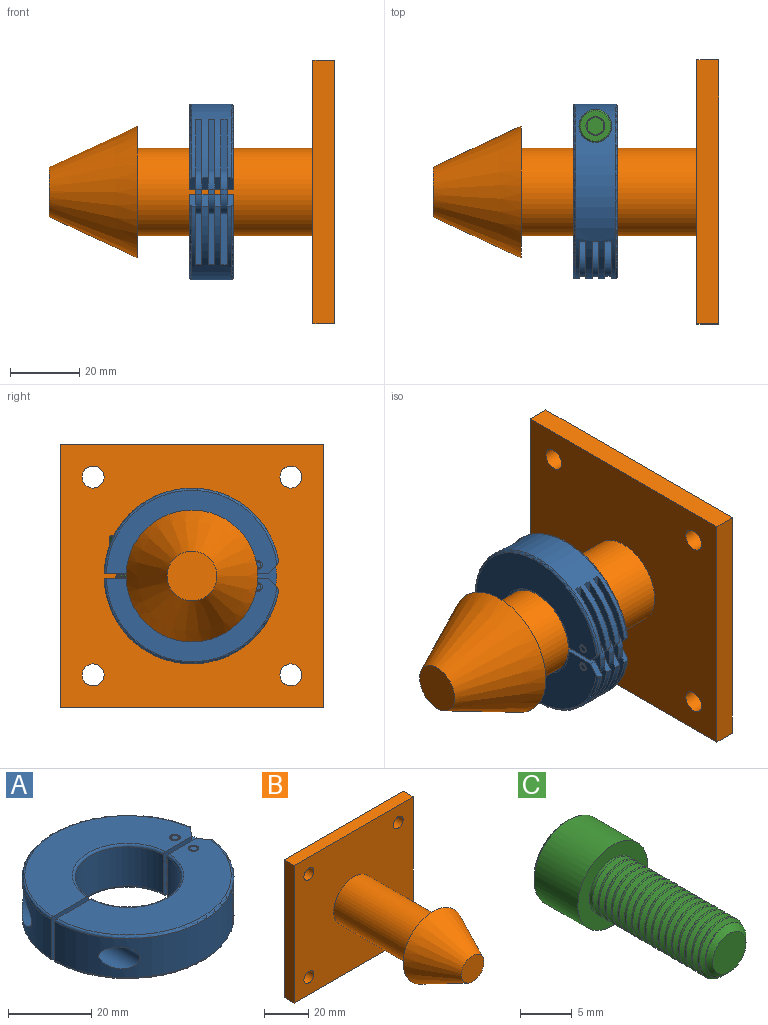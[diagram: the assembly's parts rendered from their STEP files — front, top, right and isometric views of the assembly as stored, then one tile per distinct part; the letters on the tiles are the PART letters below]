
ASSEMBLY  parts=3 mates=2
PART A: 80 faces, bbox 54.9x55.2x12.9 mm
  f0: cone r=0.89mm half-angle=45deg, axis (0,0,-1), area 3.7mm2, adj f10,f79
  f1: cone r=0.89mm half-angle=45deg, axis (0,0,1), area 3.7mm2, adj f9,f78
  f2: cone r=0.89mm half-angle=45deg, axis (0,0,-1), area 3.7mm2, adj f7,f77
  f3: cone r=0.89mm half-angle=45deg, axis (0,0,1), area 3.7mm2, adj f6,f76
  f4: cylinder r=3.17mm len=6.35mm, axis (0,-1,0), area 95mm2, adj f53,f55
  f5: cylinder r=4.76mm len=15.6mm, axis (0,-1,0), area 314.5mm2, adj f52,f55
  f6: cylinder r=1.27mm len=2.54mm, axis (0,0,-1), area 3mm2, adj f3,f51
  f7: cylinder r=1.27mm len=2.54mm, axis (0,0,-1), area 3mm2, adj f2,f50
  f8: cylinder r=3.17mm len=19.19mm, axis (0,-1,0), area 307.8mm2, adj f32,f35
  f9: cylinder r=1.27mm len=2.54mm, axis (0,0,-1), area 3mm2, adj f1,f31
  f10: cylinder r=1.27mm len=2.54mm, axis (0,0,-1), area 3mm2, adj f0,f30
  f11: plane 17.57x1.81mm, normal (1,0,0), area 31.9mm2, adj f12,f13,f32,f75
  f12: plane 18.16x10.8mm, normal (0,0,-1), area 106.4mm2, adj f11,f32,f42,f75
  f13: plane 18.16x10.8mm, normal (0,0,1), area 106.4mm2, adj f11,f32,f41,f75
  f14: plane 17.57x1.81mm, normal (1,0,0), area 31.9mm2, adj f15,f16,f52,f73
  f15: plane 18.16x10.8mm, normal (0,0,-1), area 106.4mm2, adj f14,f52,f62,f73
  f16: plane 18.16x10.8mm, normal (0,0,1), area 106.4mm2, adj f14,f52,f60,f73
  f17: plane 17.57x1.81mm, normal (1,0,0), area 31.9mm2, adj f18,f19,f32,f69
  f18: plane 18.16x10.8mm, normal (0,0,-1), area 106.4mm2, adj f17,f32,f43,f69
  f19: plane 18.16x10.8mm, normal (0,0,1), area 106.4mm2, adj f17,f32,f42,f69
  f20: plane 17.57x1.81mm, normal (1,0,0), area 31.9mm2, adj f21,f22,f52,f67
  f21: plane 18.16x10.8mm, normal (0,0,-1), area 106.4mm2, adj f20,f52,f63,f67
  f22: plane 18.16x10.8mm, normal (0,0,1), area 106.4mm2, adj f20,f52,f62,f67
  f23: cylinder r=5.35mm len=10.11mm, axis (0,0,-1), area 26.3mm2, adj f24,f25,f44,f46,f47,f48
  f24: plane 10.69x5.69mm, normal (0,0,-1), area 18.7mm2, adj f23,f26,f33,f43,f44,f45,f49,f63
  f25: plane 10.69x5.69mm, normal (0,0,1), area 18.7mm2, adj f23,f26,f33,f40,f44,f45,f49,f61
  f26: plane 1.81x1.27mm, normal (-1,0,0), area 2.3mm2, adj f24,f25,f33,f49
  f27: plane 17.57x1.81mm, normal (1,0,0), area 31.9mm2, adj f28,f29,f32,f45
  f28: plane 18.16x10.8mm, normal (0,0,1), area 106.4mm2, adj f27,f32,f43,f45
  f29: plane 18.16x10.8mm, normal (0,0,-1), area 106.4mm2, adj f27,f32,f40,f45
  f30: plane 49.29x24.13mm, normal (0,0,1), area 660.9mm2, adj f10,f33,f35,f36,f39,f40
  f31: plane 49.29x24.13mm, normal (0,0,-1), area 660.9mm2, adj f9,f33,f35,f37,f38,f41
  f32: cylinder r=25.4mm len=50.47mm, axis (0,0,-1), area 696.8mm2, adj f8,f11,f12,f13,f17,f18,f19,f27
  f33: plane 12.71x9.54mm, normal (0,1,0), area 74.5mm2, adj f24,f25,f26,f30,f31,f34,f36,f37
  f34: cylinder r=12.7mm len=25.37mm, axis (0,0,-1), area 441.5mm2, adj f33,f35,f36,f37
  f35: plane 12.72x12.71mm, normal (0,1,0), area 129.4mm2, adj f8,f30,f31,f32,f34,f36,f37,f38
  f36: torus R=13.33mm, axis (0,0,1), area 39.3mm2, adj f30,f33,f34,f35
  f37: torus R=13.33mm, axis (0,0,1), area 39.3mm2, adj f31,f33,f34,f35
  f38: torus R=24.77mm, axis (0,0,1), area 74.5mm2, adj f31,f32,f35,f41
  f39: torus R=24.77mm, axis (0,0,1), area 74.5mm2, adj f30,f32,f35,f40
  f40: plane 3.63x3.08mm, normal (0.77,0.64,0), area 8mm2, adj f25,f29,f30,f32,f33,f39
  f41: plane 3.63x3.08mm, normal (0.77,0.64,0), area 8mm2, adj f13,f31,f32,f33,f38,f72
  f42: plane 3.42x2.87mm, normal (0.77,0.64,0), area 8.1mm2, adj f12,f19,f32,f33,f66,f71
  f43: plane 3.42x2.87mm, normal (0.77,0.64,0), area 8.1mm2, adj f18,f24,f28,f32,f33,f65
  f44: plane 1.81x1.52mm, normal (1,0,0), area 2.8mm2, adj f23,f24,f25,f45
  f45: cylinder r=5.35mm len=10.11mm, axis (0,0,-1), area 26.3mm2, adj f24,f25,f27,f28,f29,f44
  f46: plane 18.16x10.8mm, normal (0,0,1), area 106.4mm2, adj f23,f48,f52,f63
  f47: plane 18.16x10.8mm, normal (0,0,-1), area 106.4mm2, adj f23,f48,f52,f61
  f48: plane 17.57x1.81mm, normal (1,0,0), area 31.9mm2, adj f23,f46,f47,f52
  f49: plane 12.71x9.54mm, normal (0,-1,0), area 74.5mm2, adj f24,f25,f26,f50,f51,f54,f56,f58
  f50: plane 49.29x24.13mm, normal (0,0,1), area 660.9mm2, adj f7,f49,f53,f56,f57,f61
  f51: plane 49.29x24.13mm, normal (0,0,-1), area 660.9mm2, adj f6,f49,f53,f58,f59,f60
  f52: cylinder r=25.4mm len=50.47mm, axis (0,0,-1), area 631.2mm2, adj f5,f14,f15,f16,f20,f21,f22,f46
  f53: plane 12.72x12.71mm, normal (0,-1,0), area 129.4mm2, adj f4,f50,f51,f52,f54,f56,f57,f58
  f54: cylinder r=12.7mm len=25.37mm, axis (0,0,-1), area 441.5mm2, adj f49,f53,f56,f58
  f55: plane 9.53x9.53mm, normal (0,1,0), area 39.6mm2, adj f4,f5
  f56: torus R=13.33mm, axis (0,0,1), area 39.3mm2, adj f49,f50,f53,f54
  f57: torus R=24.77mm, axis (0,0,1), area 74.5mm2, adj f50,f52,f53,f61
  f58: torus R=13.33mm, axis (0,0,1), area 39.3mm2, adj f49,f51,f53,f54
  f59: torus R=24.77mm, axis (0,0,1), area 74.5mm2, adj f51,f52,f53,f60
  f60: plane 3.63x3.08mm, normal (0.77,-0.64,0), area 8mm2, adj f16,f49,f51,f52,f59,f72
  f61: plane 3.63x3.08mm, normal (0.77,-0.64,0), area 8mm2, adj f25,f47,f49,f50,f52,f57
  f62: plane 3.42x2.87mm, normal (0.77,-0.64,0), area 8.1mm2, adj f15,f22,f49,f52,f66,f71
  f63: plane 3.42x2.87mm, normal (0.77,-0.64,0), area 8.1mm2, adj f21,f24,f46,f49,f52,f65
  f64: plane 1.81x1.52mm, normal (1,0,0), area 2.8mm2, adj f65,f66,f67,f69
  f65: plane 10.69x5.69mm, normal (0,0,1), area 18.7mm2, adj f33,f43,f49,f63,f64,f67,f68,f69
  f66: plane 10.69x5.69mm, normal (0,0,-1), area 18.7mm2, adj f33,f42,f49,f62,f64,f67,f68,f69
  f67: cylinder r=5.35mm len=10.11mm, axis (0,0,-1), area 26.3mm2, adj f20,f21,f22,f64,f65,f66
  f68: plane 1.81x1.27mm, normal (-1,0,0), area 2.3mm2, adj f33,f49,f65,f66
  f69: cylinder r=5.35mm len=10.11mm, axis (0,0,-1), area 26.3mm2, adj f17,f18,f19,f64,f65,f66
  f70: plane 1.81x1.52mm, normal (1,0,0), area 2.8mm2, adj f71,f72,f73,f75
  f71: plane 10.69x5.69mm, normal (0,0,1), area 18.7mm2, adj f33,f42,f49,f62,f70,f73,f74,f75
  f72: plane 10.69x5.69mm, normal (0,0,-1), area 18.7mm2, adj f33,f41,f49,f60,f70,f73,f74,f75
  f73: cylinder r=5.35mm len=10.11mm, axis (0,0,-1), area 26.3mm2, adj f14,f15,f16,f70,f71,f72
  f74: plane 1.81x1.27mm, normal (-1,0,0), area 2.3mm2, adj f33,f49,f71,f72
  f75: cylinder r=5.35mm len=10.11mm, axis (0,0,-1), area 26.3mm2, adj f11,f12,f13,f70,f71,f72
  f76: plane 1.78x1.78mm, normal (0,0,-1), area 2.5mm2, adj f3
  f77: plane 1.78x1.78mm, normal (0,0,1), area 2.5mm2, adj f2
  f78: plane 1.78x1.78mm, normal (0,0,-1), area 2.5mm2, adj f1
  f79: plane 1.78x1.78mm, normal (0,0,1), area 2.5mm2, adj f0
PART B: 14 faces, bbox 76.2x82.6x76.2 mm
  f0: cylinder r=12.7mm len=50.8mm, axis (0,1,0), area 4053.7mm2, adj f3,f9
  f1: cone r=19.05mm half-angle=25deg, axis (0,1,0), area 2311.7mm2, adj f2,f3
  f2: plane 14.41x14.41mm, normal (0,-1,0), area 163.1mm2, adj f1
  f3: plane 38.1x38.1mm, normal (0,1,0), area 633.4mm2, adj f0,f1
  f4: plane 76.2x6.35mm, normal (0,0,-1), area 483.9mm2, adj f5,f7,f8,f9
  f5: plane 76.2x6.35mm, normal (-1,0,0), area 483.9mm2, adj f4,f6,f8,f9
  f6: plane 76.2x6.35mm, normal (0,0,1), area 483.9mm2, adj f5,f7,f8,f9
  f7: plane 76.2x6.35mm, normal (1,0,0), area 483.9mm2, adj f4,f6,f8,f9
  f8: plane 76.2x76.2mm, normal (0,1,0), area 5679.8mm2, adj f4,f5,f6,f7,f10,f11,f12,f13
  f9: plane 76.2x76.2mm, normal (0,-1,0), area 5173.1mm2, adj f0,f4,f5,f6,f7,f10,f11,f12
  f10: cylinder r=3.17mm len=6.35mm, axis (0,-1,0), area 126.7mm2, adj f8,f9
  f11: cylinder r=3.17mm len=6.35mm, axis (0,-1,0), area 126.7mm2, adj f8,f9
  f12: cylinder r=3.17mm len=6.35mm, axis (0,-1,0), area 126.7mm2, adj f8,f9
  f13: cylinder r=3.17mm len=6.35mm, axis (0,-1,0), area 126.7mm2, adj f8,f9
PART C: 39 faces, bbox 10.6x23.3x10.6 mm
  f0: cone r=2.27mm half-angle=45deg, axis (0,1,0), area 15.9mm2, adj f3,f22,f36,f37,f38
  f1: cone r=4.76mm half-angle=45deg, axis (0,-1,0), area 15.5mm2, adj f19,f20
  f2: cone r=2.75mm half-angle=45deg, axis (0,1,0), area 0.7mm2, adj f20,f30
  f3: cylinder r=3.17mm len=6.35mm, axis (0,-1,0), area 3.7mm2, adj f0,f4,f36,f37
  f4: cylinder r=3.17mm len=6.35mm, axis (0,-1,0), area 4.2mm2, adj f3,f5,f36,f37
  f5: cylinder r=3.17mm len=6.35mm, axis (0,-1,0), area 4.2mm2, adj f4,f6,f36,f37
  f6: cylinder r=3.17mm len=6.35mm, axis (0,-1,0), area 4.2mm2, adj f5,f7,f36,f37
  f7: cylinder r=3.17mm len=6.35mm, axis (0,-1,0), area 4.2mm2, adj f6,f8,f36,f37
  f8: cylinder r=3.17mm len=6.35mm, axis (0,-1,0), area 4.2mm2, adj f7,f9,f36,f37
  f9: cylinder r=3.17mm len=6.35mm, axis (0,-1,0), area 4.2mm2, adj f8,f10,f36,f37
  f10: cylinder r=3.17mm len=6.35mm, axis (0,-1,0), area 4.2mm2, adj f9,f11,f36,f37
  f11: cylinder r=3.17mm len=6.35mm, axis (0,-1,0), area 4.2mm2, adj f10,f12,f36,f37
  f12: cylinder r=3.17mm len=6.35mm, axis (0,-1,0), area 4.2mm2, adj f11,f13,f36,f37
  f13: cylinder r=3.17mm len=6.35mm, axis (0,-1,0), area 4.2mm2, adj f12,f14,f36,f37
  f14: cylinder r=3.17mm len=6.35mm, axis (0,-1,0), area 4.2mm2, adj f13,f15,f36,f37
  f15: cylinder r=3.17mm len=6.35mm, axis (0,-1,0), area 4.2mm2, adj f14,f16,f36,f37
  f16: cylinder r=3.17mm len=6.35mm, axis (0,-1,0), area 4.2mm2, adj f15,f17,f36,f37
  f17: cylinder r=3.17mm len=6.35mm, axis (0,-1,0), area 4.2mm2, adj f16,f18,f36,f37
  f18: cylinder r=3.17mm len=6.35mm, axis (0,-1,0), area 12.4mm2, adj f17,f21,f35,f36,f37
  f19: cylinder r=4.76mm len=9.53mm, axis (0,-1,0), area 178.6mm2, adj f1,f21
  f20: plane 8.76x8.76mm, normal (0,1,0), area 36.6mm2, adj f1,f2,f23,f24,f25,f26,f27
  f21: plane 9.53x9.53mm, normal (0,-1,0), area 39.6mm2, adj f18,f19
  f22: plane 4.54x4.54mm, normal (0,-1,0), area 16.2mm2, adj f0
  f23: cone r=2.75mm half-angle=45deg, axis (0,1,0), area 0mm2, adj f20,f29
  f24: cone r=2.75mm half-angle=45deg, axis (0,1,0), area 0mm2, adj f20,f31
  f25: cone r=2.75mm half-angle=45deg, axis (0,1,0), area 0mm2, adj f20,f32
  f26: cone r=2.75mm half-angle=45deg, axis (0,1,0), area 0mm2, adj f20,f33
  f27: cone r=2.75mm half-angle=45deg, axis (0,1,0), area 0mm2, adj f20,f34
  f28: plane 5.5x4.76mm, normal (0,1,0), area 19.6mm2, adj f29,f30,f31,f32,f33,f34
  f29: plane 4.22x3.42mm, normal (0.5,0,0.87), area 8.1mm2, adj f23,f28,f30,f34
  f30: plane 3.44x3.02mm, normal (1,0,0), area 8.1mm2, adj f2,f28,f29,f31
  f31: plane 4.22x3.42mm, normal (0.5,0,-0.87), area 8.1mm2, adj f24,f28,f30,f32
  f32: plane 4.22x3.42mm, normal (-0.5,0,-0.87), area 8.1mm2, adj f25,f28,f31,f33
  f33: plane 4.22x3.79mm, normal (-1,0,0), area 8.1mm2, adj f26,f28,f32,f34
  f34: plane 4.22x3.42mm, normal (-0.5,0,0.87), area 8.1mm2, adj f27,f28,f29,f33
  f35: plane 0.69x0.51mm, normal (-0.09,0,1), area 0.2mm2, adj f18,f36,f37,f38
  f36: bspline ~15.38x6.56mm, area 175.9mm2, adj f0,f3,f4,f5,f6,f7,f8,f9
  f37: bspline ~15.49x6.56mm, area 181.3mm2, adj f0,f3,f4,f5,f6,f7,f8,f9
  f38: cylinder r=2.66mm len=15.17mm, axis (0,-1,0), area 46.3mm2, adj f0,f35,f36,f37
PLACE A rot(axis=(0.58,-0.58,-0.58),120deg) t=(-35.66,0,0)mm
PLACE B rot(axis=(0.58,0.58,-0.58),120deg) t=(-6.35,0,0)mm
PLACE C rot(axis=(0,0.71,0.71),180deg) t=(-54.71,19.05,0)mm
MATE fastened C.f0 <-> A.f4  axis (0,0,-1) through (-35.66,19.05,5.4)mm
MATE slider A.f32 <-> B.f0  axis (1,0,0) through (-29.95,0,0)mm
